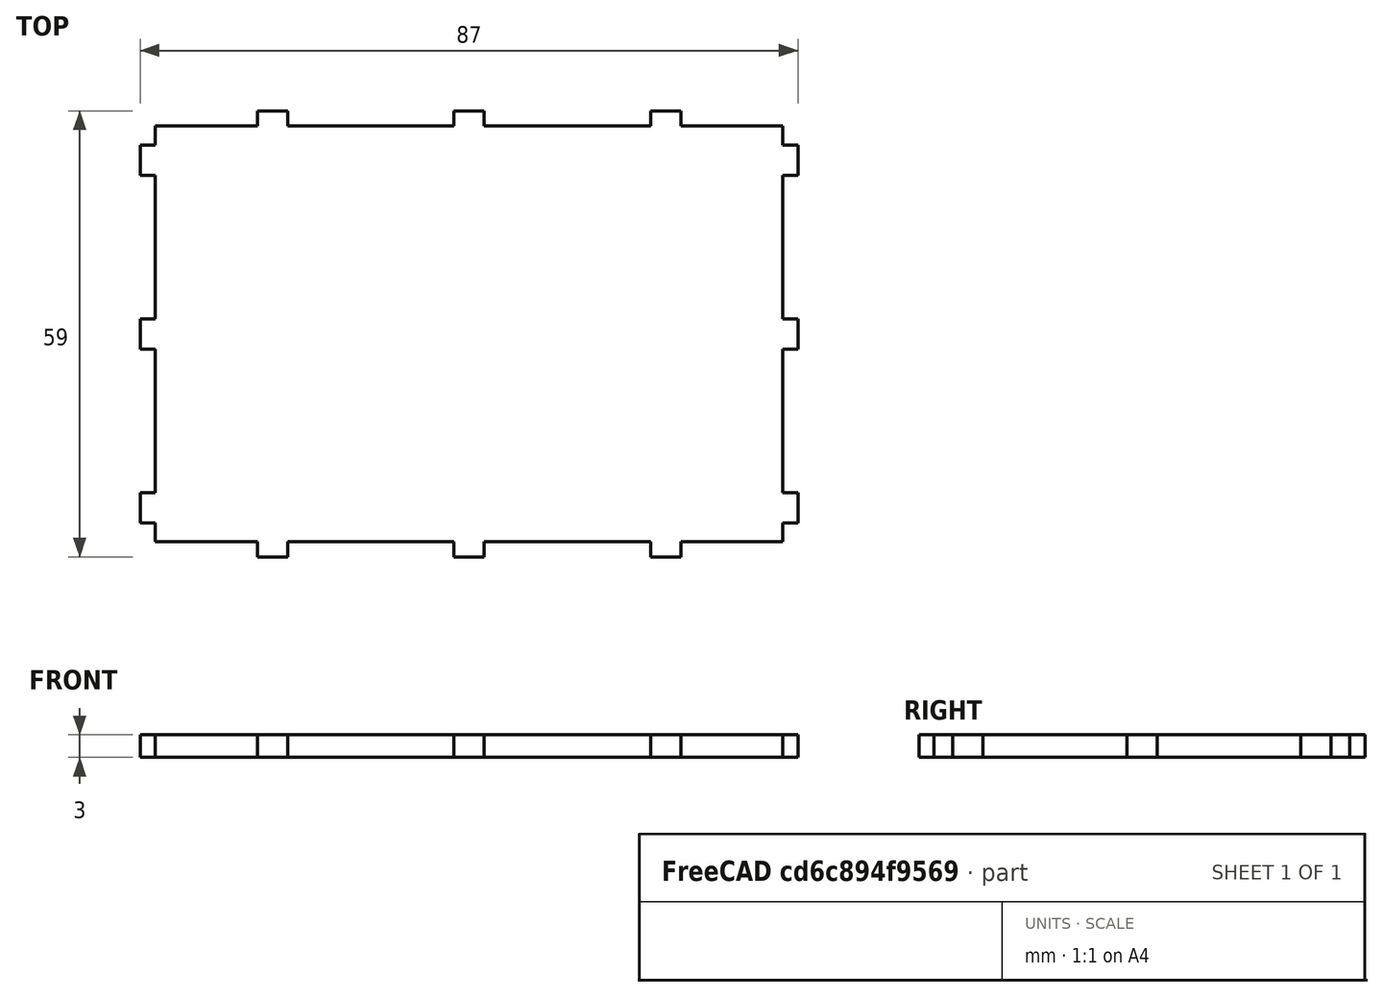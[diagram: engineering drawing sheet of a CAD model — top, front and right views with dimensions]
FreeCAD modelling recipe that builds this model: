
FCSTD DOCUMENT  (FreeCAD 0.17R13522 (Git))
Label: cortador matrizia
License: CreativeCommons Attribution-ShareAlike
LicenseURL: http://creativecommons.org/licenses/by-sa/4.0/
objects: Part::Fuse×12, Part::Feature×11, Part::Box×3, Part::Part2DObjectPython×2
note: 28 computed .brp shape members not serialized (recipe doc carries the construction recipe); baked Part::Feature solids carry a one-line shape summary decoded from their .brp

FEATURE [Part::Box] Box  label="Cube"
  AttacherType = Attacher::AttachEngine3D
  Height = 3
  Length = 83
  Width = 55
FEATURE [Part::Box] Box001  label="Cube001"
  AttacherType = Attacher::AttachEngine3D
  Height = 3
  Length = 2
  Placement = pos=(-2,2.5,0) rot=(0,0,1;0rad)
  Width = 4
FEATURE [Part::Feature] Box001001  label="Cube002"
  Placement = pos=(-2,48.5,0) rot=(0,0,1;0rad)
  shape: bbox 2 x 4 x 3 mm, 6 faces (baked)
FEATURE [Part::Feature] Box001001001  label="Cube003"
  Placement = pos=(-2,25.5,0) rot=(0,0,1;0rad)
  shape: bbox 2 x 4 x 3 mm, 6 faces (baked)
FEATURE [Part::Part2DObjectPython] Line002  # Draft 2D object (typed FeaturePython)
  ChamferSize = 0
  Closed = false
  End = (-1,27.5,3)
  FilletRadius = 0
  Length = 42.5
  MakeFace = true
  Points = (2) [(41.5,27.5,3),(-1,27.5,3)]
  Start = (41.5,27.5,3)
  Subdivisions = 0
FEATURE [Part::Part2DObjectPython] Line003  # Draft 2D object (typed FeaturePython)
  ChamferSize = 0
  Closed = false
  End = (41.5,54.8504,3)
  FilletRadius = 0
  Length = 27.3504
  MakeFace = true
  Points = (2) [(41.5,27.5,3),(41.5,54.8504,3)]
  Start = (41.5,27.5,3)
  Subdivisions = 0
FEATURE [Part::Box] Box001001002  label="Cube004"
  AttacherType = Attacher::AttachEngine3D
  Height = 3
  Length = 4
  Placement = pos=(13.5,55,0) rot=(0,0,1;0rad)
  Width = 2
FEATURE [Part::Feature] Box001001002001  label="Cube005"
  Placement = pos=(65.5,55,0) rot=(0,0,1;0rad)
  shape: bbox 4 x 2 x 3 mm, 6 faces (baked)
FEATURE [Part::Feature] Box001001002002  label="Cube006"
  Placement = pos=(39.5,55,0) rot=(0,0,1;0rad)
  shape: bbox 4 x 2 x 3 mm, 6 faces (baked)
FEATURE [Part::Feature] Box001001002001001  label="Cube007"
  Placement = pos=(65.5,-2,0) rot=(0,0,1;0rad)
  shape: bbox 4 x 2 x 3 mm, 6 faces (baked)
FEATURE [Part::Feature] Box001001002002001  label="Cube008"
  Placement = pos=(39.5,-2,0) rot=(0,0,1;0rad)
  shape: bbox 4 x 2 x 3 mm, 6 faces (baked)
FEATURE [Part::Feature] Box001001002002002  label="Cube009"
  Placement = pos=(13.5,-2,0) rot=(0,0,1;0rad)
  shape: bbox 4 x 2 x 3 mm, 6 faces (baked)
FEATURE [Part::Feature] Box001001002002003  label="Cube010"
  Placement = pos=(83,2.5,0) rot=(0,0,1;0rad)
  shape: bbox 2 x 4 x 3 mm, 6 faces (baked)
FEATURE [Part::Feature] Box001001001001  label="Cube011"
  Placement = pos=(83,25.5,0) rot=(0,0,1;0rad)
  shape: bbox 2 x 4 x 3 mm, 6 faces (baked)
FEATURE [Part::Feature] Box001001002002004  label="Cube012"
  Placement = pos=(83,48.5,0) rot=(0,0,1;0rad)
  shape: bbox 2 x 4 x 3 mm, 6 faces (baked)
FEATURE [Part::Fuse] Fusion
  Base = -> Box
  Refine = true
  Tool = -> Box001
FEATURE [Part::Fuse] Fusion001
  Base = -> Box001001001
  Refine = true
  Tool = -> Fusion
FEATURE [Part::Fuse] Fusion002
  Base = -> Box001001
  Refine = true
  Tool = -> Fusion001
FEATURE [Part::Fuse] Fusion003
  Base = -> Box001001002
  Refine = true
  Tool = -> Fusion002
FEATURE [Part::Fuse] Fusion004
  Base = -> Box001001002002
  Refine = true
  Tool = -> Fusion003
FEATURE [Part::Fuse] Fusion005
  Base = -> Box001001002001
  Refine = true
  Tool = -> Fusion004
FEATURE [Part::Fuse] Fusion006
  Base = -> Box001001002002004
  Refine = true
  Tool = -> Fusion005
FEATURE [Part::Fuse] Fusion007
  Base = -> Box001001001001
  Refine = true
  Tool = -> Fusion006
FEATURE [Part::Fuse] Fusion008
  Base = -> Box001001002002003
  Refine = true
  Tool = -> Fusion007
FEATURE [Part::Fuse] Fusion009
  Base = -> Box001001002001001
  Refine = true
  Tool = -> Fusion008
FEATURE [Part::Fuse] Fusion010
  Base = -> Box001001002002001
  Refine = true
  Tool = -> Fusion009
FEATURE [Part::Fuse] Fusion011  label="cortador matrizia"
  Base = -> Box001001002002002
  Refine = true
  Tool = -> Fusion010
FEATURE [Part::Feature] Fusion011001  label="cortador matrizia001"
  shape: bbox 87 x 59 x 3 mm, 54 faces (baked)
